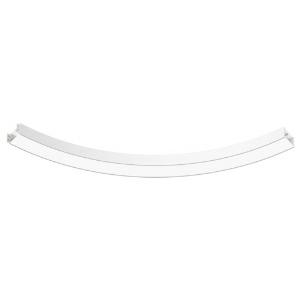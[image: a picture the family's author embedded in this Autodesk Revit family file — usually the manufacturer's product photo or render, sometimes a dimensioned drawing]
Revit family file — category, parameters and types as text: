
# Revit family: super-g_super-g__4000___72deg_hl_led__36_8w_5680lm_3000k_cri_80_430-1110_744d
name_source: partatom
category: Leuchten
revit_build: Autodesk Revit 2016 (Build: 20190508_0715(x64)
units: mm (PartAtom-declared; Revit-internal decimal feet)

## family parameters
Basisbauteil = Fläche
Beim Laden mit Abzugskörper schneiden = Nein
Bemaßung runder Anschluss = Durchmesser verwenden
Gemeinsam genutzt = Nein
Lichtquelle = Nein
Raumberechnungspunkt = Nein
Teiletyp = Normal

## types (1)
- 430-1110- (1 x LED, 710 lm, 3000K)
    Approval mark = CE
    Beschreibung = The insert consists of aluminum-extruded profile. Charming SOFT-EDGE design ensure unparalleled styling. The ballast is integrated and allows for an operation with 220-240V (50/60Hz). SUPER-G (# 430-1110) ist not dimmable (on/off).
    CIE Flux Codes = 44 75 94 100 65
    Color Rendering = 1B/80…89
    Color Temperature = 3000K
    Height = 120 mm
    Hersteller = Prolicht
    Lamp Light Flux = 710 lm
    Lamp count = 1
    Lampe = 1 x LED
    Length = 314 mm
    Luminous efficacy = 90 lm/W
    ModVariant = Nein
    Modell = 430-1110
    Mounting Place = Ceiling
    Mounting Type = Pendant
    Number of Poles = 1
    OnlyDefault = Ja
    Power Factor = 1
    Product Name = SUPER-G__SUPER-G  4000 / 72° HL LED: 36,8W 5680lm 3000K CRI:80
    Product group = Suspended profile systems
    ProductGroupID = 944
    Protection Class = Protection class I
    Protection Degree = IP 20
    RLX_Detail_Level = 1
    RlxData = <blob elided: 29405 chars, md5=9bd9d44a>
    Scheinlast = 41 VA
    Socket = socket
    Standby Power = 0 W
    System Light Flux = 3692 lm
    System Power = 41 W
    Typenbild = 430-1110.jpg
    URL = http://relux.com
    VarID = 430-1110-
    Voltage = 0 V
    Vorgabe-Ansicht = 1800 mm
    Weight = 0.00 kg
    Width = 150 mm

## geometry (parser evidence)
native form markers: Blend x4, Sweep x29
no freeform markers — native parametric forms only
